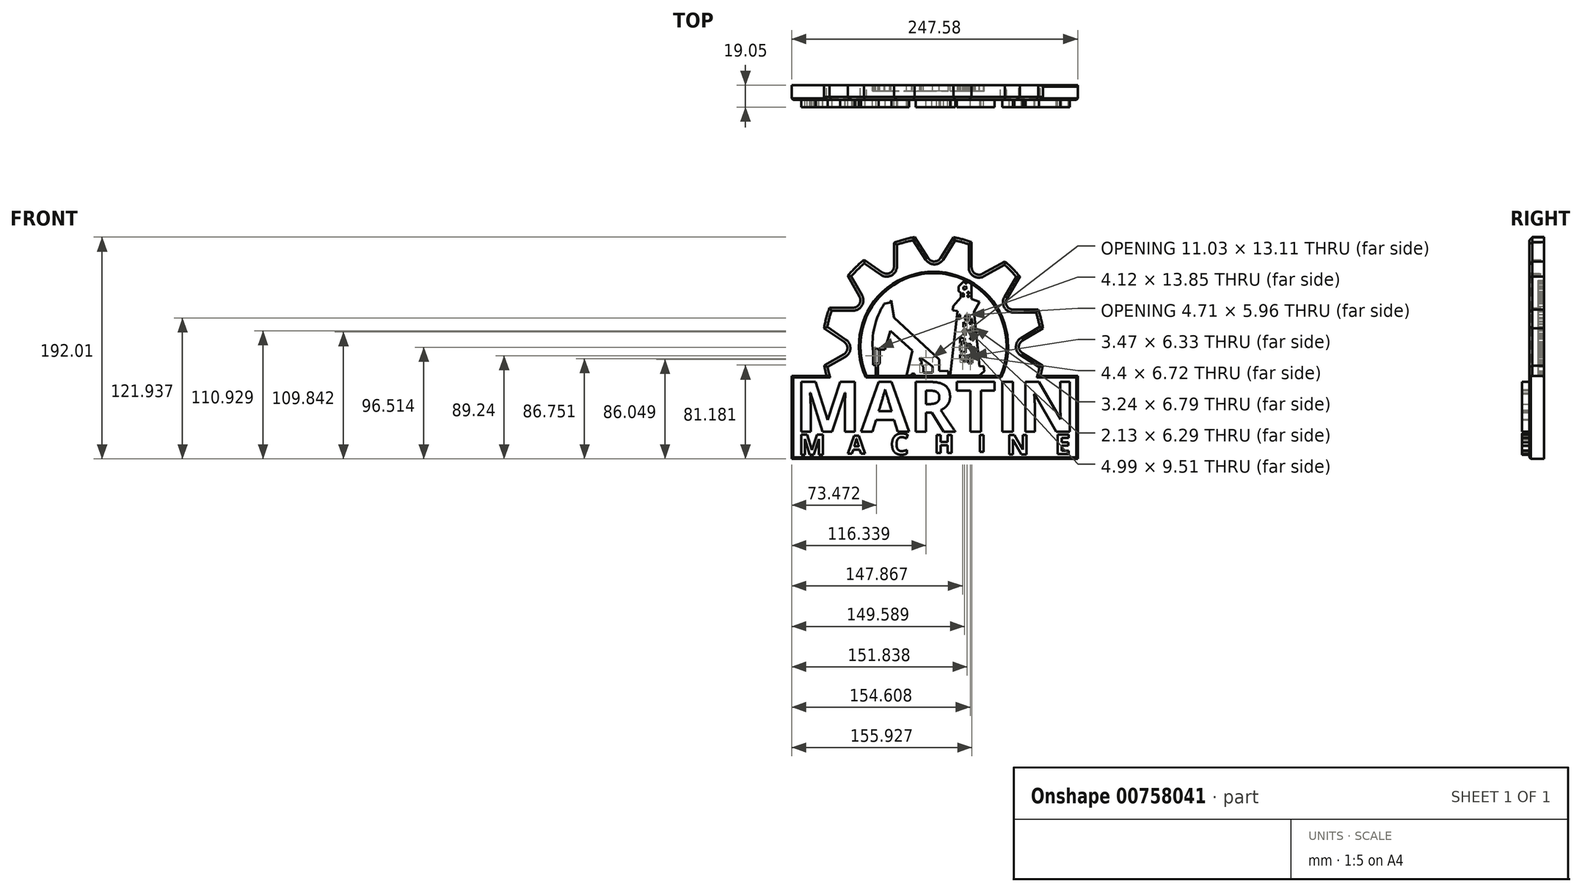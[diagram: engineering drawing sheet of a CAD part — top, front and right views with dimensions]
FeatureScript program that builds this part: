
annotation { "Feature Type Name" : "Feature", "Feature Type Description" : "" }
export const myFeature = defineFeature(function(context is Context, id is Id, definition is map)
    precondition{}
    {
        {
            var Q0;
            Q0=qCreatedBy(makeId("Front.planeOp"),FACE);
            var sketch = newSketch(context, id + "F0", { "sketchPlane" : qUnion([Q0])});
            skLineSegment(sketch, "E0.bottom", {"start": v(-69.87, -72.17) * mm, "end": v(-39.57, -72.17) * mm});
            skLineSegment(sketch, "E0.top", {"start": v(-69.87, -143.83) * mm, "end": v(177.7, -143.83) * mm});
            skLineSegment(sketch, "E0.left", {"start": v(-69.87, -72.17) * mm, "end": v(-69.87, -143.83) * mm});
            skLineSegment(sketch, "E0.right", {"start": v(177.7, -72.17) * mm, "end": v(177.7, -143.83) * mm});
            skArc(sketch, "E1", {"start": v(110.75, -72.17) * mm, "mid": v(52.91, 16.92) * mm, "end": v(-4.93, -72.17) * mm});
            skArc(sketch, "E2", {"start": v(145.39, -72.17) * mm, "mid": v(146.53, -67.65) * mm, "end": v(147.45, -63.07) * mm});
            skLineSegment(sketch, "E3.trimOffspring", {"start": v(-4.93, -72.17) * mm, "end": v(110.75, -72.17) * mm});
            skLineSegment(sketch, "E4.trimOffspring", {"start": v(145.39, -72.17) * mm, "end": v(177.7, -72.17) * mm});
            skLineSegment(sketch, "E5", {"start": v(-41.66, -62.9) * mm, "end": v(-24.87, -53.45) * mm});
            skLineSegment(sketch, "E6", {"start": v(-24.42, -42.66) * mm, "end": v(-41.82, -30.86) * mm});
            skLineSegment(sketch, "E7", {"start": v(-37.09, -13) * mm, "end": v(-16.73, -13) * mm});
            skLineSegment(sketch, "E8", {"start": v(-11.2, -3.53) * mm, "end": v(-21.33, 14.47) * mm});
            skLineSegment(sketch, "E9", {"start": v(-7.17, 28.47) * mm, "end": v(8.76, 17.56) * mm});
            skLineSegment(sketch, "E10", {"start": v(18.7, 22.8) * mm, "end": v(18.7, 43.3) * mm});
            skLineSegment(sketch, "E11", {"start": v(36.5, 48.18) * mm, "end": v(48.3, 29.98) * mm});
            skLineSegment(sketch, "E12", {"start": v(59.01, 30.05) * mm, "end": v(70.3, 48) * mm});
            skLineSegment(sketch, "E13", {"start": v(85.92, 43.74) * mm, "end": v(85.92, 21.91) * mm});
            skLineSegment(sketch, "E14", {"start": v(95.34, 16.35) * mm, "end": v(114.73, 27.04) * mm});
            skLineSegment(sketch, "E15", {"start": v(127.68, 13.8) * mm, "end": v(116.4, -4.98) * mm});
            skLineSegment(sketch, "E16", {"start": v(121.85, -14.6) * mm, "end": v(143.5, -14.6) * mm});
            skLineSegment(sketch, "E17", {"start": v(147.62, -30.7) * mm, "end": v(129.87, -41.41) * mm});
            skLineSegment(sketch, "E18", {"start": v(129.83, -52.26) * mm, "end": v(147.45, -63.07) * mm});
            skPoint(sketch, "E19.visualSharp", {"position": v(-15.93, -48.41) * mm});
            skArc(sketch, "E19.filletArc", {"start": v(-24.87, -53.45) * mm, "mid": v(-21.64, -48.18) * mm, "end": v(-24.42, -42.66) * mm});
            skPoint(sketch, "E20.visualSharp", {"position": v(-5.86, -13) * mm});
            skArc(sketch, "E20.filletArc", {"start": v(-16.73, -13) * mm, "mid": v(-11.25, -9.85) * mm, "end": v(-11.2, -3.53) * mm});
            skPoint(sketch, "E21.visualSharp", {"position": v(18.7, 10.76) * mm});
            skArc(sketch, "E21.filletArc", {"start": v(8.76, 17.56) * mm, "mid": v(15.3, 17.19) * mm, "end": v(18.7, 22.8) * mm});
            skPoint(sketch, "E22.visualSharp", {"position": v(53.72, 21.63) * mm});
            skArc(sketch, "E22.filletArc", {"start": v(48.3, 29.98) * mm, "mid": v(53.68, 27.08) * mm, "end": v(59.01, 30.05) * mm});
            skPoint(sketch, "E23.visualSharp", {"position": v(85.92, 11.16) * mm});
            skArc(sketch, "E23.filletArc", {"start": v(85.92, 21.91) * mm, "mid": v(89.04, 16.45) * mm, "end": v(95.34, 16.35) * mm});
            skPoint(sketch, "E24.visualSharp", {"position": v(110.64, -14.6) * mm});
            skArc(sketch, "E24.filletArc", {"start": v(116.4, -4.98) * mm, "mid": v(116.33, -11.38) * mm, "end": v(121.85, -14.6) * mm});
            skPoint(sketch, "E25.visualSharp", {"position": v(120.94, -46.8) * mm});
            skArc(sketch, "E25.filletArc", {"start": v(129.87, -41.41) * mm, "mid": v(126.8, -46.83) * mm, "end": v(129.83, -52.26) * mm});
            skArc(sketch, "E26.trimOffspring", {"start": v(-41.66, -62.9) * mm, "mid": v(-40.73, -67.56) * mm, "end": v(-39.57, -72.17) * mm});
            skArc(sketch, "E27.trimOffspring", {"start": v(-37.09, -13) * mm, "mid": v(-39.89, -21.81) * mm, "end": v(-41.82, -30.86) * mm});
            skArc(sketch, "E28.trimOffspring", {"start": v(-7.17, 28.47) * mm, "mid": v(-14.61, 21.84) * mm, "end": v(-21.33, 14.47) * mm});
            skArc(sketch, "E29.trimOffspring", {"start": v(36.5, 48.18) * mm, "mid": v(27.48, 46.17) * mm, "end": v(18.7, 43.3) * mm});
            skArc(sketch, "E30.trimOffspring", {"start": v(85.92, 43.74) * mm, "mid": v(78.2, 46.2) * mm, "end": v(70.3, 48) * mm});
            skArc(sketch, "E31.trimOffspring", {"start": v(127.68, 13.8) * mm, "mid": v(121.53, 20.74) * mm, "end": v(114.73, 27.04) * mm});
            skArc(sketch, "E32.trimOffspring", {"start": v(147.62, -30.7) * mm, "mid": v(145.9, -22.56) * mm, "end": v(143.5, -14.6) * mm});
            skSolve(sketch);
        }
        {
            var Q0;
            Q0=makeQuery(id+"F0.imprint","IMPRINT",FACE,{"disambiguationData":[TD([[makeQuery(id+"F0.imprint","IMPRINT",EDGE,{"derivedFrom":sQuery(id+"F0.wireOp",EDGE,"E0.bottom")}),-1.0]])]});
            extrude(context, id + "F1", {"entities" : qUnion([Q0]), "depth" : 12.7 * mm, "offsetDistance" : 25.4 * mm});
        }
        {
            var Q0;
            Q0=makeQuery(id+"F1.opExtrude","CAP_FACE",FACE,{"disambiguationData":[OSD([sQuery(id+"F0.wireOp",EDGE,"E0.bottom"),sQuery(id+"F0.wireOp",EDGE,"E0.top"),sQuery(id+"F0.wireOp",EDGE,"E0.left"),sQuery(id+"F0.wireOp",EDGE,"E0.right"),sQuery(id+"F0.wireOp",EDGE,"E1"),sQuery(id+"F0.wireOp",EDGE,"E2"),sQuery(id+"F0.wireOp",EDGE,"E3.trimOffspring"),sQuery(id+"F0.wireOp",EDGE,"E4.trimOffspring"),sQuery(id+"F0.wireOp",EDGE,"E5"),sQuery(id+"F0.wireOp",EDGE,"E6"),sQuery(id+"F0.wireOp",EDGE,"E7"),sQuery(id+"F0.wireOp",EDGE,"E8"),sQuery(id+"F0.wireOp",EDGE,"E9"),sQuery(id+"F0.wireOp",EDGE,"E10"),sQuery(id+"F0.wireOp",EDGE,"E11"),sQuery(id+"F0.wireOp",EDGE,"E12"),sQuery(id+"F0.wireOp",EDGE,"E13"),sQuery(id+"F0.wireOp",EDGE,"E14"),sQuery(id+"F0.wireOp",EDGE,"E15"),sQuery(id+"F0.wireOp",EDGE,"E16"),sQuery(id+"F0.wireOp",EDGE,"E17"),sQuery(id+"F0.wireOp",EDGE,"E18"),sQuery(id+"F0.wireOp",EDGE,"E19.filletArc"),sQuery(id+"F0.wireOp",EDGE,"E20.filletArc"),sQuery(id+"F0.wireOp",EDGE,"E21.filletArc"),sQuery(id+"F0.wireOp",EDGE,"E22.filletArc"),sQuery(id+"F0.wireOp",EDGE,"E23.filletArc"),sQuery(id+"F0.wireOp",EDGE,"E24.filletArc"),sQuery(id+"F0.wireOp",EDGE,"E25.filletArc"),sQuery(id+"F0.wireOp",EDGE,"E26.trimOffspring"),sQuery(id+"F0.wireOp",EDGE,"E27.trimOffspring"),sQuery(id+"F0.wireOp",EDGE,"E28.trimOffspring"),sQuery(id+"F0.wireOp",EDGE,"E29.trimOffspring"),sQuery(id+"F0.wireOp",EDGE,"E30.trimOffspring"),sQuery(id+"F0.wireOp",EDGE,"E31.trimOffspring"),sQuery(id+"F0.wireOp",EDGE,"E32.trimOffspring")])],"isStart":false});
            var sketch = newSketch(context, id + "F2", { "sketchPlane" : qUnion([Q0])});
            skText(sketch, "E33", { "text": "MARTIN", "fontName": "OpenSans-Bold.ttf"});
            const initialGuessF2  = {"E33": [-0.06698, -0.12048, 1, 0, 0.04361]};
            skSetInitialGuess(sketch, initialGuessF2);
            skSolve(sketch);
        }
        {
            var Q0;
            Q0=makeQuery(id+"F2.imprint","IMPRINT",FACE,{"disambiguationData":[TD([[makeQuery(id+"F2.imprint","IMPRINT",EDGE,{"derivedFrom":sQuery(id+"F2.wireOp",EDGE,"E33.sketch_text.stroke-0")}),-1.0]])]});
            var Q1;
            Q1=makeQuery(id+"F2.imprint","IMPRINT",FACE,{"disambiguationData":[TD([[makeQuery(id+"F2.imprint","IMPRINT",EDGE,{"derivedFrom":sQuery(id+"F2.wireOp",EDGE,"E33.sketch_text.stroke-19")}),-1.0]])]});
            var Q2;
            Q2=makeQuery(id+"F2.imprint","IMPRINT",FACE,{"disambiguationData":[TD([[makeQuery(id+"F2.imprint","IMPRINT",EDGE,{"derivedFrom":sQuery(id+"F2.wireOp",EDGE,"E33.sketch_text.stroke-31")}),-1.0]])]});
            var Q3;
            Q3=makeQuery(id+"F2.imprint","IMPRINT",FACE,{"disambiguationData":[TD([[makeQuery(id+"F2.imprint","IMPRINT",EDGE,{"derivedFrom":sQuery(id+"F2.wireOp",EDGE,"E33.sketch_text.stroke-50")}),-1.0]])]});
            var Q4;
            Q4=makeQuery(id+"F2.imprint","IMPRINT",FACE,{"disambiguationData":[TD([[makeQuery(id+"F2.imprint","IMPRINT",EDGE,{"derivedFrom":sQuery(id+"F2.wireOp",EDGE,"E33.sketch_text.stroke-58")}),-1.0]])]});
            var Q5;
            Q5=makeQuery(id+"F2.imprint","IMPRINT",FACE,{"disambiguationData":[TD([[makeQuery(id+"F2.imprint","IMPRINT",EDGE,{"derivedFrom":sQuery(id+"F2.wireOp",EDGE,"E33.sketch_text.stroke-62")}),-1.0]])]});
            extrude(context, id + "F3", {"entities" : qUnion([Q0, Q1, Q2, Q3, Q4, Q5]), "operationType" : NewBodyOperationType.ADD, "depth" : 6.35 * mm, "offsetDistance" : 25.4 * mm});
        }
        {
            var Q0;
            {var subQ0=sQuery(id+"F0.wireOp",EDGE,"E15");var subQ1=sQuery(id+"F0.wireOp",EDGE,"E14");var subQ2=sQuery(id+"F0.wireOp",EDGE,"E12");var subQ3=sQuery(id+"F0.wireOp",EDGE,"E11");var subQ4=sQuery(id+"F0.wireOp",EDGE,"E10");var subQ5=sQuery(id+"F0.wireOp",EDGE,"E9");var subQ6=sQuery(id+"F0.wireOp",EDGE,"E8");var subQ7=sQuery(id+"F0.wireOp",EDGE,"E7");var subQ8=sQuery(id+"F0.wireOp",EDGE,"E0.left");var subQ9=sQuery(id+"F0.wireOp",EDGE,"E0.top");var subQ10=sQuery(id+"F0.wireOp",EDGE,"E0.right");var subQ11=sQuery(id+"F0.wireOp",EDGE,"E0.bottom");var subQ12=sQuery(id+"F0.wireOp",EDGE,"E6");var subQ13=sQuery(id+"F0.wireOp",EDGE,"E1");var subQ14=sQuery(id+"F0.wireOp",EDGE,"E2");var subQ15=sQuery(id+"F0.wireOp",EDGE,"E3.trimOffspring");var subQ16=sQuery(id+"F0.wireOp",EDGE,"E4.trimOffspring");var subQ17=sQuery(id+"F0.wireOp",EDGE,"E5");var subQ18=sQuery(id+"F0.wireOp",EDGE,"E13");var subQ19=sQuery(id+"F0.wireOp",EDGE,"E22.filletArc");var subQ20=sQuery(id+"F0.wireOp",EDGE,"E25.filletArc");var subQ21=sQuery(id+"F0.wireOp",EDGE,"E26.trimOffspring");var subQ22=sQuery(id+"F0.wireOp",EDGE,"E16");var subQ23=sQuery(id+"F0.wireOp",EDGE,"E27.trimOffspring");var subQ24=sQuery(id+"F0.wireOp",EDGE,"E17");var subQ25=sQuery(id+"F0.wireOp",EDGE,"E28.trimOffspring");var subQ26=sQuery(id+"F0.wireOp",EDGE,"E18");var subQ27=sQuery(id+"F0.wireOp",EDGE,"E29.trimOffspring");var subQ28=sQuery(id+"F0.wireOp",EDGE,"E19.filletArc");var subQ29=sQuery(id+"F0.wireOp",EDGE,"E30.trimOffspring");var subQ30=sQuery(id+"F0.wireOp",EDGE,"E20.filletArc");var subQ31=sQuery(id+"F0.wireOp",EDGE,"E31.trimOffspring");var subQ32=sQuery(id+"F0.wireOp",EDGE,"E21.filletArc");var subQ33=sQuery(id+"F0.wireOp",EDGE,"E32.trimOffspring");var subQ34=sQuery(id+"F0.wireOp",EDGE,"E23.filletArc");var subQ35=sQuery(id+"F0.wireOp",EDGE,"E24.filletArc");Q0=makeQuery(id+"F3.boolean.opBoolean","SPLIT",FACE,{"disambiguationData":[TD([makeQuery(id+"F1.opExtrude","SWEPT_FACE",FACE,{"disambiguationData":[OSD([subQ11])]})])],"derivedFrom":makeQuery(id+"F1.opExtrude","CAP_FACE",FACE,{"disambiguationData":[OSD([subQ11,subQ9,subQ8,subQ10,subQ13,subQ14,subQ15,subQ16,subQ17,subQ12,subQ7,subQ6,subQ5,subQ4,subQ3,subQ2,subQ18,subQ1,subQ0,subQ22,subQ24,subQ26,subQ28,subQ30,subQ32,subQ19,subQ34,subQ35,subQ20,subQ21,subQ23,subQ25,subQ27,subQ29,subQ31,subQ33])],"isStart":false})});}
            var sketch = newSketch(context, id + "F4", { "sketchPlane" : qUnion([Q0])});
            skText(sketch, "E34", { "text": "M", "fontName": "OpenSans-Bold.ttf"});
            const initialGuessF4  = {"E34": [-0.06372, -0.14035, 1, 0, 0.0175]};
            skSetInitialGuess(sketch, initialGuessF4);
            skSolve(sketch);
        }
        {
            var Q0;
            Q0 = qSketchRegion(id + "F4", true);
            extrude(context, id + "F5", {"entities" : qUnion([Q0]), "operationType" : NewBodyOperationType.ADD, "depth" : 6.35 * mm, "offsetDistance" : 25.4 * mm});
        }
        {
            var Q0;
            {var subQ0=sQuery(id+"F0.wireOp",EDGE,"E15");var subQ1=sQuery(id+"F0.wireOp",EDGE,"E14");var subQ2=sQuery(id+"F0.wireOp",EDGE,"E12");var subQ3=sQuery(id+"F0.wireOp",EDGE,"E11");var subQ4=sQuery(id+"F0.wireOp",EDGE,"E10");var subQ5=sQuery(id+"F0.wireOp",EDGE,"E9");var subQ6=sQuery(id+"F0.wireOp",EDGE,"E8");var subQ7=sQuery(id+"F0.wireOp",EDGE,"E7");var subQ8=sQuery(id+"F0.wireOp",EDGE,"E0.left");var subQ9=sQuery(id+"F0.wireOp",EDGE,"E0.top");var subQ10=sQuery(id+"F0.wireOp",EDGE,"E0.right");var subQ11=sQuery(id+"F0.wireOp",EDGE,"E0.bottom");var subQ12=sQuery(id+"F0.wireOp",EDGE,"E6");var subQ13=sQuery(id+"F0.wireOp",EDGE,"E1");var subQ14=sQuery(id+"F0.wireOp",EDGE,"E2");var subQ15=sQuery(id+"F0.wireOp",EDGE,"E3.trimOffspring");var subQ16=sQuery(id+"F0.wireOp",EDGE,"E4.trimOffspring");var subQ17=sQuery(id+"F0.wireOp",EDGE,"E5");var subQ18=sQuery(id+"F0.wireOp",EDGE,"E13");var subQ19=sQuery(id+"F0.wireOp",EDGE,"E22.filletArc");var subQ20=sQuery(id+"F0.wireOp",EDGE,"E25.filletArc");var subQ21=sQuery(id+"F0.wireOp",EDGE,"E26.trimOffspring");var subQ22=sQuery(id+"F0.wireOp",EDGE,"E16");var subQ23=sQuery(id+"F0.wireOp",EDGE,"E27.trimOffspring");var subQ24=sQuery(id+"F0.wireOp",EDGE,"E17");var subQ25=sQuery(id+"F0.wireOp",EDGE,"E28.trimOffspring");var subQ26=sQuery(id+"F0.wireOp",EDGE,"E18");var subQ27=sQuery(id+"F0.wireOp",EDGE,"E29.trimOffspring");var subQ28=sQuery(id+"F0.wireOp",EDGE,"E19.filletArc");var subQ29=sQuery(id+"F0.wireOp",EDGE,"E30.trimOffspring");var subQ30=sQuery(id+"F0.wireOp",EDGE,"E20.filletArc");var subQ31=sQuery(id+"F0.wireOp",EDGE,"E31.trimOffspring");var subQ32=sQuery(id+"F0.wireOp",EDGE,"E21.filletArc");var subQ33=sQuery(id+"F0.wireOp",EDGE,"E32.trimOffspring");var subQ34=sQuery(id+"F0.wireOp",EDGE,"E23.filletArc");var subQ35=sQuery(id+"F0.wireOp",EDGE,"E24.filletArc");Q0=makeQuery(id+"F3.boolean.opBoolean","SPLIT",FACE,{"disambiguationData":[TD([makeQuery(id+"F1.opExtrude","SWEPT_FACE",FACE,{"disambiguationData":[OSD([subQ11])]})])],"derivedFrom":makeQuery(id+"F1.opExtrude","CAP_FACE",FACE,{"disambiguationData":[OSD([subQ11,subQ9,subQ8,subQ10,subQ13,subQ14,subQ15,subQ16,subQ17,subQ12,subQ7,subQ6,subQ5,subQ4,subQ3,subQ2,subQ18,subQ1,subQ0,subQ22,subQ24,subQ26,subQ28,subQ30,subQ32,subQ19,subQ34,subQ35,subQ20,subQ21,subQ23,subQ25,subQ27,subQ29,subQ31,subQ33])],"isStart":false})});}
            var sketch = newSketch(context, id + "F6", { "sketchPlane" : qUnion([Q0])});
            skText(sketch, "E35", { "text": "A", "fontName": "OpenSans-Bold.ttf"});
            const initialGuessF6  = {"E35": [-0.0213, -0.13946, 1, 0, 0.01572]};
            skSetInitialGuess(sketch, initialGuessF6);
            skSolve(sketch);
        }
        {
            var Q0;
            Q0 = qSketchRegion(id + "F6", true);
            extrude(context, id + "F7", {"entities" : qUnion([Q0]), "operationType" : NewBodyOperationType.ADD, "depth" : 6.35 * mm, "offsetDistance" : 25.4 * mm});
        }
        {
            var Q0;
            {var subQ40=sQuery(id+"F0.wireOp",EDGE,"E15");var subQ42=sQuery(id+"F0.wireOp",EDGE,"E14");var subQ44=sQuery(id+"F0.wireOp",EDGE,"E12");var subQ46=sQuery(id+"F0.wireOp",EDGE,"E11");var subQ48=sQuery(id+"F0.wireOp",EDGE,"E10");var subQ50=sQuery(id+"F0.wireOp",EDGE,"E9");var subQ52=sQuery(id+"F0.wireOp",EDGE,"E8");var subQ54=sQuery(id+"F0.wireOp",EDGE,"E7");var subQ56=sQuery(id+"F0.wireOp",EDGE,"E0.left");var subQ59=sQuery(id+"F0.wireOp",EDGE,"E0.top");var subQ61=sQuery(id+"F0.wireOp",EDGE,"E0.right");var subQ64=sQuery(id+"F0.wireOp",EDGE,"E0.bottom");var subQ65=makeQuery(id+"F1.opExtrude","SWEPT_FACE",FACE,{"disambiguationData":[OSD([subQ64])]});var subQ66=sQuery(id+"F0.wireOp",EDGE,"E6");var subQ68=sQuery(id+"F0.wireOp",EDGE,"E1");var subQ70=sQuery(id+"F0.wireOp",EDGE,"E2");var subQ72=sQuery(id+"F0.wireOp",EDGE,"E3.trimOffspring");var subQ74=sQuery(id+"F0.wireOp",EDGE,"E4.trimOffspring");var subQ76=sQuery(id+"F0.wireOp",EDGE,"E5");var subQ78=sQuery(id+"F0.wireOp",EDGE,"E13");var subQ81=sQuery(id+"F0.wireOp",EDGE,"E22.filletArc");var subQ84=sQuery(id+"F0.wireOp",EDGE,"E25.filletArc");var subQ88=sQuery(id+"F0.wireOp",EDGE,"E26.trimOffspring");var subQ91=sQuery(id+"F0.wireOp",EDGE,"E16");var subQ94=sQuery(id+"F0.wireOp",EDGE,"E27.trimOffspring");var subQ97=sQuery(id+"F0.wireOp",EDGE,"E17");var subQ100=sQuery(id+"F0.wireOp",EDGE,"E28.trimOffspring");var subQ103=sQuery(id+"F0.wireOp",EDGE,"E18");var subQ106=sQuery(id+"F0.wireOp",EDGE,"E29.trimOffspring");var subQ109=sQuery(id+"F0.wireOp",EDGE,"E19.filletArc");var subQ112=sQuery(id+"F0.wireOp",EDGE,"E30.trimOffspring");var subQ115=sQuery(id+"F0.wireOp",EDGE,"E20.filletArc");var subQ118=sQuery(id+"F0.wireOp",EDGE,"E31.trimOffspring");var subQ121=sQuery(id+"F0.wireOp",EDGE,"E21.filletArc");var subQ124=sQuery(id+"F0.wireOp",EDGE,"E32.trimOffspring");var subQ127=sQuery(id+"F0.wireOp",EDGE,"E23.filletArc");var subQ129=sQuery(id+"F0.wireOp",EDGE,"E24.filletArc");Q0=makeQuery(id+"F7.boolean.opBoolean","SPLIT",FACE,{"disambiguationData":[TD([subQ65])],"derivedFrom":makeQuery(id+"F3.boolean.opBoolean","SPLIT",FACE,{"disambiguationData":[TD([subQ65])],"derivedFrom":makeQuery(id+"F1.opExtrude","CAP_FACE",FACE,{"disambiguationData":[OSD([subQ64,subQ59,subQ56,subQ61,subQ68,subQ70,subQ72,subQ74,subQ76,subQ66,subQ54,subQ52,subQ50,subQ48,subQ46,subQ44,subQ78,subQ42,subQ40,subQ91,subQ97,subQ103,subQ109,subQ115,subQ121,subQ81,subQ127,subQ129,subQ84,subQ88,subQ94,subQ100,subQ106,subQ112,subQ118,subQ124])],"isStart":false})})});}
            var sketch = newSketch(context, id + "F8", { "sketchPlane" : qUnion([Q0])});
            skText(sketch, "E36", { "text": "C", "fontName": "OpenSans-Bold.ttf"});
            const initialGuessF8  = {"E36": [0.0155, -0.14006, 1, 0, 0.0181]};
            skSetInitialGuess(sketch, initialGuessF8);
            skSolve(sketch);
        }
        {
            var Q0;
            Q0 = qSketchRegion(id + "F8", true);
            extrude(context, id + "F9", {"entities" : qUnion([Q0]), "operationType" : NewBodyOperationType.ADD, "depth" : 6.35 * mm, "offsetDistance" : 25.4 * mm});
        }
        {
            var Q0;
            {var subQ40=sQuery(id+"F0.wireOp",EDGE,"E15");var subQ42=sQuery(id+"F0.wireOp",EDGE,"E14");var subQ44=sQuery(id+"F0.wireOp",EDGE,"E12");var subQ46=sQuery(id+"F0.wireOp",EDGE,"E11");var subQ48=sQuery(id+"F0.wireOp",EDGE,"E10");var subQ50=sQuery(id+"F0.wireOp",EDGE,"E9");var subQ52=sQuery(id+"F0.wireOp",EDGE,"E8");var subQ54=sQuery(id+"F0.wireOp",EDGE,"E7");var subQ56=sQuery(id+"F0.wireOp",EDGE,"E0.left");var subQ59=sQuery(id+"F0.wireOp",EDGE,"E0.top");var subQ61=sQuery(id+"F0.wireOp",EDGE,"E0.right");var subQ64=sQuery(id+"F0.wireOp",EDGE,"E0.bottom");var subQ65=makeQuery(id+"F1.opExtrude","SWEPT_FACE",FACE,{"disambiguationData":[OSD([subQ64])]});var subQ66=sQuery(id+"F0.wireOp",EDGE,"E6");var subQ68=sQuery(id+"F0.wireOp",EDGE,"E1");var subQ70=sQuery(id+"F0.wireOp",EDGE,"E2");var subQ72=sQuery(id+"F0.wireOp",EDGE,"E3.trimOffspring");var subQ74=sQuery(id+"F0.wireOp",EDGE,"E4.trimOffspring");var subQ76=sQuery(id+"F0.wireOp",EDGE,"E5");var subQ78=sQuery(id+"F0.wireOp",EDGE,"E13");var subQ81=sQuery(id+"F0.wireOp",EDGE,"E22.filletArc");var subQ84=sQuery(id+"F0.wireOp",EDGE,"E25.filletArc");var subQ88=sQuery(id+"F0.wireOp",EDGE,"E26.trimOffspring");var subQ91=sQuery(id+"F0.wireOp",EDGE,"E16");var subQ94=sQuery(id+"F0.wireOp",EDGE,"E27.trimOffspring");var subQ97=sQuery(id+"F0.wireOp",EDGE,"E17");var subQ100=sQuery(id+"F0.wireOp",EDGE,"E28.trimOffspring");var subQ103=sQuery(id+"F0.wireOp",EDGE,"E18");var subQ106=sQuery(id+"F0.wireOp",EDGE,"E29.trimOffspring");var subQ109=sQuery(id+"F0.wireOp",EDGE,"E19.filletArc");var subQ112=sQuery(id+"F0.wireOp",EDGE,"E30.trimOffspring");var subQ115=sQuery(id+"F0.wireOp",EDGE,"E20.filletArc");var subQ118=sQuery(id+"F0.wireOp",EDGE,"E31.trimOffspring");var subQ121=sQuery(id+"F0.wireOp",EDGE,"E21.filletArc");var subQ124=sQuery(id+"F0.wireOp",EDGE,"E32.trimOffspring");var subQ127=sQuery(id+"F0.wireOp",EDGE,"E23.filletArc");var subQ129=sQuery(id+"F0.wireOp",EDGE,"E24.filletArc");Q0=makeQuery(id+"F7.boolean.opBoolean","SPLIT",FACE,{"disambiguationData":[TD([subQ65])],"derivedFrom":makeQuery(id+"F3.boolean.opBoolean","SPLIT",FACE,{"disambiguationData":[TD([subQ65])],"derivedFrom":makeQuery(id+"F1.opExtrude","CAP_FACE",FACE,{"disambiguationData":[OSD([subQ64,subQ59,subQ56,subQ61,subQ68,subQ70,subQ72,subQ74,subQ76,subQ66,subQ54,subQ52,subQ50,subQ48,subQ46,subQ44,subQ78,subQ42,subQ40,subQ91,subQ97,subQ103,subQ109,subQ115,subQ121,subQ81,subQ127,subQ129,subQ84,subQ88,subQ94,subQ100,subQ106,subQ112,subQ118,subQ124])],"isStart":false})})});}
            var sketch = newSketch(context, id + "F10", { "sketchPlane" : qUnion([Q0])});
            skText(sketch, "E37", { "text": "H", "fontName": "OpenSans-Bold.ttf"});
            const initialGuessF10  = {"E37": [0.05377, -0.13887, 1, 0, 0.01572]};
            skSetInitialGuess(sketch, initialGuessF10);
            skSolve(sketch);
        }
        {
            var Q0;
            Q0 = qSketchRegion(id + "F10", true);
            extrude(context, id + "F11", {"entities" : qUnion([Q0]), "operationType" : NewBodyOperationType.ADD, "depth" : 6.35 * mm, "offsetDistance" : 25.4 * mm});
        }
        {
            var Q0;
            {var subQ40=sQuery(id+"F0.wireOp",EDGE,"E15");var subQ42=sQuery(id+"F0.wireOp",EDGE,"E14");var subQ44=sQuery(id+"F0.wireOp",EDGE,"E12");var subQ46=sQuery(id+"F0.wireOp",EDGE,"E11");var subQ48=sQuery(id+"F0.wireOp",EDGE,"E10");var subQ50=sQuery(id+"F0.wireOp",EDGE,"E9");var subQ52=sQuery(id+"F0.wireOp",EDGE,"E8");var subQ54=sQuery(id+"F0.wireOp",EDGE,"E7");var subQ56=sQuery(id+"F0.wireOp",EDGE,"E0.left");var subQ59=sQuery(id+"F0.wireOp",EDGE,"E0.top");var subQ61=sQuery(id+"F0.wireOp",EDGE,"E0.right");var subQ64=sQuery(id+"F0.wireOp",EDGE,"E0.bottom");var subQ65=makeQuery(id+"F1.opExtrude","SWEPT_FACE",FACE,{"disambiguationData":[OSD([subQ64])]});var subQ66=sQuery(id+"F0.wireOp",EDGE,"E6");var subQ68=sQuery(id+"F0.wireOp",EDGE,"E1");var subQ70=sQuery(id+"F0.wireOp",EDGE,"E2");var subQ72=sQuery(id+"F0.wireOp",EDGE,"E3.trimOffspring");var subQ74=sQuery(id+"F0.wireOp",EDGE,"E4.trimOffspring");var subQ76=sQuery(id+"F0.wireOp",EDGE,"E5");var subQ78=sQuery(id+"F0.wireOp",EDGE,"E13");var subQ81=sQuery(id+"F0.wireOp",EDGE,"E22.filletArc");var subQ84=sQuery(id+"F0.wireOp",EDGE,"E25.filletArc");var subQ88=sQuery(id+"F0.wireOp",EDGE,"E26.trimOffspring");var subQ91=sQuery(id+"F0.wireOp",EDGE,"E16");var subQ94=sQuery(id+"F0.wireOp",EDGE,"E27.trimOffspring");var subQ97=sQuery(id+"F0.wireOp",EDGE,"E17");var subQ100=sQuery(id+"F0.wireOp",EDGE,"E28.trimOffspring");var subQ103=sQuery(id+"F0.wireOp",EDGE,"E18");var subQ106=sQuery(id+"F0.wireOp",EDGE,"E29.trimOffspring");var subQ109=sQuery(id+"F0.wireOp",EDGE,"E19.filletArc");var subQ112=sQuery(id+"F0.wireOp",EDGE,"E30.trimOffspring");var subQ115=sQuery(id+"F0.wireOp",EDGE,"E20.filletArc");var subQ118=sQuery(id+"F0.wireOp",EDGE,"E31.trimOffspring");var subQ121=sQuery(id+"F0.wireOp",EDGE,"E21.filletArc");var subQ124=sQuery(id+"F0.wireOp",EDGE,"E32.trimOffspring");var subQ127=sQuery(id+"F0.wireOp",EDGE,"E23.filletArc");var subQ129=sQuery(id+"F0.wireOp",EDGE,"E24.filletArc");Q0=makeQuery(id+"F7.boolean.opBoolean","SPLIT",FACE,{"disambiguationData":[TD([subQ65])],"derivedFrom":makeQuery(id+"F3.boolean.opBoolean","SPLIT",FACE,{"disambiguationData":[TD([subQ65])],"derivedFrom":makeQuery(id+"F1.opExtrude","CAP_FACE",FACE,{"disambiguationData":[OSD([subQ64,subQ59,subQ56,subQ61,subQ68,subQ70,subQ72,subQ74,subQ76,subQ66,subQ54,subQ52,subQ50,subQ48,subQ46,subQ44,subQ78,subQ42,subQ40,subQ91,subQ97,subQ103,subQ109,subQ115,subQ121,subQ81,subQ127,subQ129,subQ84,subQ88,subQ94,subQ100,subQ106,subQ112,subQ118,subQ124])],"isStart":false})})});}
            var sketch = newSketch(context, id + "F12", { "sketchPlane" : qUnion([Q0])});
            skText(sketch, "E38", { "text": "I", "fontName": "OpenSans-Bold.ttf"});
            const initialGuessF12  = {"E38": [0.09122, -0.13776, 1, 0, 0.01454]};
            skSetInitialGuess(sketch, initialGuessF12);
            skSolve(sketch);
        }
        {
            var Q0;
            Q0=makeQuery(id+"F12.imprint","IMPRINT",FACE,{"disambiguationData":[TD([[makeQuery(id+"F12.imprint","IMPRINT",EDGE,{"derivedFrom":sQuery(id+"F12.wireOp",EDGE,"E38.sketch_text.stroke-0")}),-1.0]])]});
            extrude(context, id + "F13", {"entities" : qUnion([Q0]), "operationType" : NewBodyOperationType.ADD, "depth" : 6.35 * mm, "offsetDistance" : 25.4 * mm});
        }
        {
            var Q0;
            {var subQ40=sQuery(id+"F0.wireOp",EDGE,"E15");var subQ42=sQuery(id+"F0.wireOp",EDGE,"E14");var subQ44=sQuery(id+"F0.wireOp",EDGE,"E12");var subQ46=sQuery(id+"F0.wireOp",EDGE,"E11");var subQ48=sQuery(id+"F0.wireOp",EDGE,"E10");var subQ50=sQuery(id+"F0.wireOp",EDGE,"E9");var subQ52=sQuery(id+"F0.wireOp",EDGE,"E8");var subQ54=sQuery(id+"F0.wireOp",EDGE,"E7");var subQ56=sQuery(id+"F0.wireOp",EDGE,"E0.left");var subQ59=sQuery(id+"F0.wireOp",EDGE,"E0.top");var subQ61=sQuery(id+"F0.wireOp",EDGE,"E0.right");var subQ64=sQuery(id+"F0.wireOp",EDGE,"E0.bottom");var subQ65=makeQuery(id+"F1.opExtrude","SWEPT_FACE",FACE,{"disambiguationData":[OSD([subQ64])]});var subQ66=sQuery(id+"F0.wireOp",EDGE,"E6");var subQ68=sQuery(id+"F0.wireOp",EDGE,"E1");var subQ70=sQuery(id+"F0.wireOp",EDGE,"E2");var subQ72=sQuery(id+"F0.wireOp",EDGE,"E3.trimOffspring");var subQ74=sQuery(id+"F0.wireOp",EDGE,"E4.trimOffspring");var subQ76=sQuery(id+"F0.wireOp",EDGE,"E5");var subQ78=sQuery(id+"F0.wireOp",EDGE,"E13");var subQ81=sQuery(id+"F0.wireOp",EDGE,"E22.filletArc");var subQ84=sQuery(id+"F0.wireOp",EDGE,"E25.filletArc");var subQ88=sQuery(id+"F0.wireOp",EDGE,"E26.trimOffspring");var subQ91=sQuery(id+"F0.wireOp",EDGE,"E16");var subQ94=sQuery(id+"F0.wireOp",EDGE,"E27.trimOffspring");var subQ97=sQuery(id+"F0.wireOp",EDGE,"E17");var subQ100=sQuery(id+"F0.wireOp",EDGE,"E28.trimOffspring");var subQ103=sQuery(id+"F0.wireOp",EDGE,"E18");var subQ106=sQuery(id+"F0.wireOp",EDGE,"E29.trimOffspring");var subQ109=sQuery(id+"F0.wireOp",EDGE,"E19.filletArc");var subQ112=sQuery(id+"F0.wireOp",EDGE,"E30.trimOffspring");var subQ115=sQuery(id+"F0.wireOp",EDGE,"E20.filletArc");var subQ118=sQuery(id+"F0.wireOp",EDGE,"E31.trimOffspring");var subQ121=sQuery(id+"F0.wireOp",EDGE,"E21.filletArc");var subQ124=sQuery(id+"F0.wireOp",EDGE,"E32.trimOffspring");var subQ127=sQuery(id+"F0.wireOp",EDGE,"E23.filletArc");var subQ129=sQuery(id+"F0.wireOp",EDGE,"E24.filletArc");Q0=makeQuery(id+"F7.boolean.opBoolean","SPLIT",FACE,{"disambiguationData":[TD([subQ65])],"derivedFrom":makeQuery(id+"F3.boolean.opBoolean","SPLIT",FACE,{"disambiguationData":[TD([subQ65])],"derivedFrom":makeQuery(id+"F1.opExtrude","CAP_FACE",FACE,{"disambiguationData":[OSD([subQ64,subQ59,subQ56,subQ61,subQ68,subQ70,subQ72,subQ74,subQ76,subQ66,subQ54,subQ52,subQ50,subQ48,subQ46,subQ44,subQ78,subQ42,subQ40,subQ91,subQ97,subQ103,subQ109,subQ115,subQ121,subQ81,subQ127,subQ129,subQ84,subQ88,subQ94,subQ100,subQ106,subQ112,subQ118,subQ124])],"isStart":false})})});}
            var sketch = newSketch(context, id + "F14", { "sketchPlane" : qUnion([Q0])});
            skText(sketch, "E39", { "text": "N", "fontName": "OpenSans-Bold.ttf"});
            const initialGuessF14  = {"E39": [0.11641, -0.13995, 1, 0, 0.01678]};
            skSetInitialGuess(sketch, initialGuessF14);
            skSolve(sketch);
        }
        {
            var Q0;
            Q0=makeQuery(id+"F14.imprint","IMPRINT",FACE,{"disambiguationData":[TD([[makeQuery(id+"F14.imprint","IMPRINT",EDGE,{"derivedFrom":sQuery(id+"F14.wireOp",EDGE,"E39.sketch_text.stroke-0")}),-1.0]])]});
            extrude(context, id + "F15", {"entities" : qUnion([Q0]), "operationType" : NewBodyOperationType.ADD, "depth" : 6.35 * mm, "offsetDistance" : 25.4 * mm});
        }
        {
            var Q0;
            {var subQ40=sQuery(id+"F0.wireOp",EDGE,"E15");var subQ42=sQuery(id+"F0.wireOp",EDGE,"E14");var subQ44=sQuery(id+"F0.wireOp",EDGE,"E12");var subQ46=sQuery(id+"F0.wireOp",EDGE,"E11");var subQ48=sQuery(id+"F0.wireOp",EDGE,"E10");var subQ50=sQuery(id+"F0.wireOp",EDGE,"E9");var subQ52=sQuery(id+"F0.wireOp",EDGE,"E8");var subQ54=sQuery(id+"F0.wireOp",EDGE,"E7");var subQ56=sQuery(id+"F0.wireOp",EDGE,"E0.left");var subQ59=sQuery(id+"F0.wireOp",EDGE,"E0.top");var subQ61=sQuery(id+"F0.wireOp",EDGE,"E0.right");var subQ64=sQuery(id+"F0.wireOp",EDGE,"E0.bottom");var subQ65=makeQuery(id+"F1.opExtrude","SWEPT_FACE",FACE,{"disambiguationData":[OSD([subQ64])]});var subQ66=sQuery(id+"F0.wireOp",EDGE,"E6");var subQ68=sQuery(id+"F0.wireOp",EDGE,"E1");var subQ70=sQuery(id+"F0.wireOp",EDGE,"E2");var subQ72=sQuery(id+"F0.wireOp",EDGE,"E3.trimOffspring");var subQ74=sQuery(id+"F0.wireOp",EDGE,"E4.trimOffspring");var subQ76=sQuery(id+"F0.wireOp",EDGE,"E5");var subQ78=sQuery(id+"F0.wireOp",EDGE,"E13");var subQ81=sQuery(id+"F0.wireOp",EDGE,"E22.filletArc");var subQ84=sQuery(id+"F0.wireOp",EDGE,"E25.filletArc");var subQ88=sQuery(id+"F0.wireOp",EDGE,"E26.trimOffspring");var subQ91=sQuery(id+"F0.wireOp",EDGE,"E16");var subQ94=sQuery(id+"F0.wireOp",EDGE,"E27.trimOffspring");var subQ97=sQuery(id+"F0.wireOp",EDGE,"E17");var subQ100=sQuery(id+"F0.wireOp",EDGE,"E28.trimOffspring");var subQ103=sQuery(id+"F0.wireOp",EDGE,"E18");var subQ106=sQuery(id+"F0.wireOp",EDGE,"E29.trimOffspring");var subQ109=sQuery(id+"F0.wireOp",EDGE,"E19.filletArc");var subQ112=sQuery(id+"F0.wireOp",EDGE,"E30.trimOffspring");var subQ115=sQuery(id+"F0.wireOp",EDGE,"E20.filletArc");var subQ118=sQuery(id+"F0.wireOp",EDGE,"E31.trimOffspring");var subQ121=sQuery(id+"F0.wireOp",EDGE,"E21.filletArc");var subQ124=sQuery(id+"F0.wireOp",EDGE,"E32.trimOffspring");var subQ127=sQuery(id+"F0.wireOp",EDGE,"E23.filletArc");var subQ129=sQuery(id+"F0.wireOp",EDGE,"E24.filletArc");Q0=makeQuery(id+"F7.boolean.opBoolean","SPLIT",FACE,{"disambiguationData":[TD([subQ65])],"derivedFrom":makeQuery(id+"F3.boolean.opBoolean","SPLIT",FACE,{"disambiguationData":[TD([subQ65])],"derivedFrom":makeQuery(id+"F1.opExtrude","CAP_FACE",FACE,{"disambiguationData":[OSD([subQ64,subQ59,subQ56,subQ61,subQ68,subQ70,subQ72,subQ74,subQ76,subQ66,subQ54,subQ52,subQ50,subQ48,subQ46,subQ44,subQ78,subQ42,subQ40,subQ91,subQ97,subQ103,subQ109,subQ115,subQ121,subQ81,subQ127,subQ129,subQ84,subQ88,subQ94,subQ100,subQ106,subQ112,subQ118,subQ124])],"isStart":false})})});}
            var sketch = newSketch(context, id + "F16", { "sketchPlane" : qUnion([Q0])});
            skText(sketch, "E40", { "text": "E", "fontName": "OpenSans-Bold.ttf"});
            const initialGuessF16  = {"E40": [0.15816, -0.13974, 1, 0, 0.017]};
            skSetInitialGuess(sketch, initialGuessF16);
            skSolve(sketch);
        }
        {
            var Q0;
            Q0 = qSketchRegion(id + "F16", true);
            extrude(context, id + "F17", {"entities" : qUnion([Q0]), "operationType" : NewBodyOperationType.ADD, "depth" : 6.35 * mm, "offsetDistance" : 25.4 * mm});
        }
        {
            var Q0;
            Q0=makeQuery(id+"F1.opExtrude","CAP_EDGE",EDGE,{"disambiguationData":[OSD([sQuery(id+"F0.wireOp",EDGE,"E27.trimOffspring")])],"isStart":false});
            var Q1;
            Q1=makeQuery(id+"F1.opExtrude","CAP_EDGE",EDGE,{"disambiguationData":[OSD([sQuery(id+"F0.wireOp",EDGE,"E26.trimOffspring")])],"isStart":false});
            var Q2;
            Q2=makeQuery(id+"F1.opExtrude","CAP_EDGE",EDGE,{"disambiguationData":[OSD([sQuery(id+"F0.wireOp",EDGE,"E28.trimOffspring")])],"isStart":false});
            var Q3;
            Q3=makeQuery(id+"F1.opExtrude","CAP_EDGE",EDGE,{"disambiguationData":[OSD([sQuery(id+"F0.wireOp",EDGE,"E29.trimOffspring")])],"isStart":false});
            var Q4;
            Q4=makeQuery(id+"F1.opExtrude","CAP_EDGE",EDGE,{"disambiguationData":[OSD([sQuery(id+"F0.wireOp",EDGE,"E30.trimOffspring")])],"isStart":false});
            var Q5;
            Q5=makeQuery(id+"F1.opExtrude","CAP_EDGE",EDGE,{"disambiguationData":[OSD([sQuery(id+"F0.wireOp",EDGE,"E31.trimOffspring")])],"isStart":false});
            var Q6;
            Q6=makeQuery(id+"F1.opExtrude","CAP_EDGE",EDGE,{"disambiguationData":[OSD([sQuery(id+"F0.wireOp",EDGE,"E32.trimOffspring")])],"isStart":false});
            var Q7;
            Q7=makeQuery(id+"F1.opExtrude","CAP_EDGE",EDGE,{"disambiguationData":[OSD([sQuery(id+"F0.wireOp",EDGE,"E2")])],"isStart":false});
            chamfer(context, id + "F18", {"entities" : qUnion([Q0, Q1, Q2, Q3, Q4, Q5, Q6, Q7]), "width" : 2.54 * mm, "tangentPropagation" : true});
        }
        {
            var Q0;
            Q0=makeQuery(id+"F1.opExtrude","CAP_EDGE",EDGE,{"disambiguationData":[OSD([sQuery(id+"F0.wireOp",EDGE,"E0.bottom")])],"isStart":false});
            var Q1;
            Q1=makeQuery(id+"F1.opExtrude","CAP_EDGE",EDGE,{"disambiguationData":[OSD([sQuery(id+"F0.wireOp",EDGE,"E0.left")])],"isStart":false});
            var Q2;
            Q2=makeQuery(id+"F1.opExtrude","CAP_EDGE",EDGE,{"disambiguationData":[OSD([sQuery(id+"F0.wireOp",EDGE,"E0.top")])],"isStart":false});
            var Q3;
            Q3=makeQuery(id+"F1.opExtrude","CAP_EDGE",EDGE,{"disambiguationData":[OSD([sQuery(id+"F0.wireOp",EDGE,"E0.right")])],"isStart":false});
            var Q4;
            Q4=makeQuery(id+"F1.opExtrude","CAP_EDGE",EDGE,{"disambiguationData":[OSD([sQuery(id+"F0.wireOp",EDGE,"E4.trimOffspring")])],"isStart":true});
            var Q5;
            Q5=makeQuery(id+"F1.opExtrude","CAP_EDGE",EDGE,{"disambiguationData":[OSD([sQuery(id+"F0.wireOp",EDGE,"E4.trimOffspring")])],"isStart":false});
            chamfer(context, id + "F19", {"entities" : qUnion([Q0, Q1, Q2, Q3, Q4, Q5]), "width" : 1.27 * mm, "tangentPropagation" : true});
        }
        {
            var Q0;
            Q0=makeQuery(id+"F1.opExtrude","CAP_EDGE",EDGE,{"disambiguationData":[OSD([sQuery(id+"F0.wireOp",EDGE,"E3.trimOffspring")])],"isStart":false});
            var Q1;
            Q1=makeQuery(id+"F1.opExtrude","CAP_EDGE",EDGE,{"disambiguationData":[OSD([sQuery(id+"F0.wireOp",EDGE,"E1")])],"isStart":false});
            chamfer(context, id + "F20", {"entities" : qUnion([Q0, Q1]), "width" : 1.27 * mm, "tangentPropagation" : true});
        }
        {
            var Q0;
            Q0=makeQuery(id+"F1.opExtrude","CAP_EDGE",EDGE,{"disambiguationData":[OSD([sQuery(id+"F0.wireOp",EDGE,"E5")])],"isStart":false});
            var Q1;
            Q1=makeQuery(id+"F1.opExtrude","CAP_EDGE",EDGE,{"disambiguationData":[OSD([sQuery(id+"F0.wireOp",EDGE,"E19.filletArc")])],"isStart":false});
            var Q2;
            Q2=makeQuery(id+"F1.opExtrude","CAP_EDGE",EDGE,{"disambiguationData":[OSD([sQuery(id+"F0.wireOp",EDGE,"E7")])],"isStart":false});
            var Q3;
            Q3=makeQuery(id+"F1.opExtrude","CAP_EDGE",EDGE,{"disambiguationData":[OSD([sQuery(id+"F0.wireOp",EDGE,"E20.filletArc")])],"isStart":false});
            var Q4;
            Q4=makeQuery(id+"F1.opExtrude","CAP_EDGE",EDGE,{"disambiguationData":[OSD([sQuery(id+"F0.wireOp",EDGE,"E9")])],"isStart":false});
            var Q5;
            Q5=makeQuery(id+"F1.opExtrude","CAP_EDGE",EDGE,{"disambiguationData":[OSD([sQuery(id+"F0.wireOp",EDGE,"E21.filletArc")])],"isStart":false});
            var Q6;
            Q6=makeQuery(id+"F1.opExtrude","CAP_EDGE",EDGE,{"disambiguationData":[OSD([sQuery(id+"F0.wireOp",EDGE,"E10")])],"isStart":false});
            var Q7;
            Q7=makeQuery(id+"F1.opExtrude","CAP_EDGE",EDGE,{"disambiguationData":[OSD([sQuery(id+"F0.wireOp",EDGE,"E11")])],"isStart":false});
            var Q8;
            Q8=makeQuery(id+"F1.opExtrude","CAP_EDGE",EDGE,{"disambiguationData":[OSD([sQuery(id+"F0.wireOp",EDGE,"E13")])],"isStart":false});
            var Q9;
            Q9=makeQuery(id+"F1.opExtrude","CAP_EDGE",EDGE,{"disambiguationData":[OSD([sQuery(id+"F0.wireOp",EDGE,"E23.filletArc")])],"isStart":false});
            var Q10;
            Q10=makeQuery(id+"F1.opExtrude","CAP_EDGE",EDGE,{"disambiguationData":[OSD([sQuery(id+"F0.wireOp",EDGE,"E15")])],"isStart":false});
            var Q11;
            Q11=makeQuery(id+"F1.opExtrude","CAP_EDGE",EDGE,{"disambiguationData":[OSD([sQuery(id+"F0.wireOp",EDGE,"E24.filletArc")])],"isStart":false});
            var Q12;
            Q12=makeQuery(id+"F1.opExtrude","CAP_EDGE",EDGE,{"disambiguationData":[OSD([sQuery(id+"F0.wireOp",EDGE,"E16")])],"isStart":false});
            var Q13;
            Q13=makeQuery(id+"F1.opExtrude","CAP_EDGE",EDGE,{"disambiguationData":[OSD([sQuery(id+"F0.wireOp",EDGE,"E17")])],"isStart":false});
            var Q14;
            Q14=makeQuery(id+"F1.opExtrude","CAP_EDGE",EDGE,{"disambiguationData":[OSD([sQuery(id+"F0.wireOp",EDGE,"E25.filletArc")])],"isStart":false});
            var Q15;
            Q15=makeQuery(id+"F1.opExtrude","CAP_EDGE",EDGE,{"disambiguationData":[OSD([sQuery(id+"F0.wireOp",EDGE,"E18")])],"isStart":false});
            chamfer(context, id + "F21", {"entities" : qUnion([Q0, Q1, Q2, Q3, Q4, Q5, Q6, Q7, Q8, Q9, Q10, Q11, Q12, Q13, Q14, Q15]), "width" : 2.54 * mm, "tangentPropagation" : true});
        }
        {
            var Q0;
            Q0=qCreatedBy(makeId("Front.planeOp"),FACE);
            var sketch = newSketch(context, id + "F22", { "sketchPlane" : qUnion([Q0])});
            skLineSegment(sketch, "E41", {"start": v(51.99, -63.8) * mm, "end": v(41.6, -56.1) * mm});
            skLineSegment(sketch, "E42", {"start": v(41.6, -56.1) * mm, "end": v(40.95, -58.18) * mm});
            skLineSegment(sketch, "E43", {"start": v(40.95, -58.18) * mm, "end": v(42.7, -59.48) * mm});
            skLineSegment(sketch, "E44", {"start": v(42.7, -59.48) * mm, "end": v(42.7, -62.19) * mm});
            skLineSegment(sketch, "E45", {"start": v(42.7, -62.19) * mm, "end": v(44.26, -64.09) * mm});
            skLineSegment(sketch, "E46", {"start": v(44.26, -64.09) * mm, "end": v(44.26, -69.2) * mm});
            skLineSegment(sketch, "E47", {"start": v(44.26, -69.2) * mm, "end": v(51.98, -69.2) * mm});
            skLineSegment(sketch, "E48", {"start": v(51.98, -69.2) * mm, "end": v(51.99, -63.8) * mm});
            skLineSegment(sketch, "E49", {"start": v(57.84, -67.7) * mm, "end": v(57.84, -57.7) * mm});
            skLineSegment(sketch, "E50", {"start": v(57.84, -57.7) * mm, "end": v(18.83, -21.5) * mm});
            skLineSegment(sketch, "E51", {"start": v(18.83, -21.5) * mm, "end": v(16.3, -6.8) * mm});
            skLineSegment(sketch, "E52", {"start": v(16.3, -6.8) * mm, "end": v(15.02, -8.55) * mm});
            skLineSegment(sketch, "E53", {"start": v(15.02, -8.55) * mm, "end": v(10.2, -9.62) * mm});
            skLineSegment(sketch, "E54", {"start": v(0.53, -62.67) * mm, "end": v(2.75, -62.9) * mm});
            skLineSegment(sketch, "E55", {"start": v(2.75, -62.9) * mm, "end": v(2.75, -71.78) * mm});
            skLineSegment(sketch, "E56", {"start": v(2.75, -71.78) * mm, "end": v(4.74, -71.78) * mm});
            skLineSegment(sketch, "E57", {"start": v(4.74, -71.78) * mm, "end": v(4.74, -62.73) * mm});
            skLineSegment(sketch, "E58", {"start": v(4.74, -62.73) * mm, "end": v(6.37, -61.4) * mm});
            skLineSegment(sketch, "E59", {"start": v(6.37, -61.4) * mm, "end": v(6.37, -49.24) * mm});
            skLineSegment(sketch, "E60", {"start": v(6.37, -49.24) * mm, "end": v(10.67, -49.24) * mm});
            skLineSegment(sketch, "E61", {"start": v(10.67, -49.24) * mm, "end": v(15.57, -32.92) * mm});
            skLineSegment(sketch, "E62", {"start": v(15.57, -32.92) * mm, "end": v(34.7, -50.13) * mm});
            skLineSegment(sketch, "E63", {"start": v(34.7, -50.13) * mm, "end": v(29.5, -71.78) * mm});
            skLineSegment(sketch, "E64", {"start": v(29.5, -71.78) * mm, "end": v(33.96, -71.78) * mm});
            skLineSegment(sketch, "E65", {"start": v(33.96, -71.78) * mm, "end": v(33.96, -70.3) * mm});
            skLineSegment(sketch, "E66", {"start": v(33.96, -70.3) * mm, "end": v(36.63, -70.3) * mm});
            skLineSegment(sketch, "E67", {"start": v(36.63, -70.3) * mm, "end": v(36.63, -71.93) * mm});
            skLineSegment(sketch, "E68", {"start": v(36.63, -71.93) * mm, "end": v(65.7, -71.93) * mm});
            skLineSegment(sketch, "E69", {"start": v(65.7, -71.93) * mm, "end": v(65.7, -67.93) * mm});
            skLineSegment(sketch, "E70", {"start": v(65.7, -67.93) * mm, "end": v(57.84, -67.7) * mm});
            skLineSegment(sketch, "E71", {"start": v(0.53, -62.67) * mm, "end": v(0.53, -51.09) * mm});
            skLineSegment(sketch, "E72", {"start": v(1.54, -47.67) * mm, "end": v(1.54, -61.51) * mm});
            skLineSegment(sketch, "E73", {"start": v(1.54, -61.51) * mm, "end": v(5.66, -60.89) * mm});
            skLineSegment(sketch, "E74", {"start": v(5.66, -60.89) * mm, "end": v(5.66, -49.29) * mm});
            skLineSegment(sketch, "E75", {"start": v(5.66, -49.29) * mm, "end": v(1.54, -47.67) * mm});
            skArc(sketch, "E76", {"start": v(10.2, -9.62) * mm, "mid": v(1.82, -29.53) * mm, "end": v(0.53, -51.09) * mm});
            skSolve(sketch);
        }
        {
            var Q0;
            Q0=makeQuery(id+"F22.imprint","IMPRINT",FACE,{"disambiguationData":[TD([[makeQuery(id+"F22.imprint","IMPRINT",EDGE,{"derivedFrom":sQuery(id+"F22.wireOp",EDGE,"E41")}),-1.0]])]});
            extrude(context, id + "F23", {"entities" : qUnion([Q0]), "depth" : 5.08 * mm, "offsetDistance" : 25.4 * mm});
        }
        {
            var Q0;
            Q0=qCreatedBy(makeId("Front.planeOp"),FACE);
            var sketch = newSketch(context, id + "F24", { "sketchPlane" : qUnion([Q0])});
            skLineSegment(sketch, "E77", {"start": v(67.2, -71.8) * mm, "end": v(73.73, -15.87) * mm});
            skLineSegment(sketch, "E78", {"start": v(73.73, -15.87) * mm, "end": v(69.53, -15.38) * mm});
            skLineSegment(sketch, "E79", {"start": v(69.53, -15.38) * mm, "end": v(69.87, -11.71) * mm});
            skLineSegment(sketch, "E80", {"start": v(69.87, -11.71) * mm, "end": v(76.7, -4) * mm});
            skLineSegment(sketch, "E81", {"start": v(76.7, -4) * mm, "end": v(76.7, -0.14) * mm});
            skLineSegment(sketch, "E82", {"start": v(76.7, -0.14) * mm, "end": v(74.62, 1.34) * mm});
            skLineSegment(sketch, "E83", {"start": v(74.62, 1.34) * mm, "end": v(74.62, 5.5) * mm});
            skLineSegment(sketch, "E84", {"start": v(74.62, 5.5) * mm, "end": v(79.96, 10.83) * mm});
            skLineSegment(sketch, "E85", {"start": v(79.96, 10.83) * mm, "end": v(85.74, 7.72) * mm});
            skLineSegment(sketch, "E86", {"start": v(85.74, 7.72) * mm, "end": v(85.74, -5.48) * mm});
            skLineSegment(sketch, "E87", {"start": v(85.74, -5.48) * mm, "end": v(92.72, -7.86) * mm});
            skLineSegment(sketch, "E88", {"start": v(92.72, -7.86) * mm, "end": v(87.82, -16.46) * mm});
            skLineSegment(sketch, "E89", {"start": v(87.82, -16.46) * mm, "end": v(92.72, -63.78) * mm});
            skLineSegment(sketch, "E90", {"start": v(92.72, -63.78) * mm, "end": v(96.32, -63.4) * mm});
            skLineSegment(sketch, "E91", {"start": v(96.32, -63.4) * mm, "end": v(96.8, -68.05) * mm});
            skLineSegment(sketch, "E92", {"start": v(96.8, -68.05) * mm, "end": v(92.27, -71.8) * mm});
            skLineSegment(sketch, "E93", {"start": v(92.27, -71.8) * mm, "end": v(67.2, -71.8) * mm});
            skSolve(sketch);
        }
        {
            var Q0;
            Q0=makeQuery(id+"F24.imprint","IMPRINT",FACE,{"disambiguationData":[TD([[makeQuery(id+"F24.imprint","IMPRINT",EDGE,{"derivedFrom":sQuery(id+"F24.wireOp",EDGE,"E77")}),-1.0]])]});
            extrude(context, id + "F25", {"entities" : qUnion([Q0]), "depth" : 5.08 * mm, "offsetDistance" : 25.4 * mm});
        }
        {
            var Q0;
            Q0=makeQuery(id+"F25.opExtrude","CAP_FACE",FACE,{"disambiguationData":[OSD([sQuery(id+"F24.wireOp",EDGE,"E77"),sQuery(id+"F24.wireOp",EDGE,"E78"),sQuery(id+"F24.wireOp",EDGE,"E79"),sQuery(id+"F24.wireOp",EDGE,"E80"),sQuery(id+"F24.wireOp",EDGE,"E81"),sQuery(id+"F24.wireOp",EDGE,"E82"),sQuery(id+"F24.wireOp",EDGE,"E83"),sQuery(id+"F24.wireOp",EDGE,"E84"),sQuery(id+"F24.wireOp",EDGE,"E85"),sQuery(id+"F24.wireOp",EDGE,"E86"),sQuery(id+"F24.wireOp",EDGE,"E87"),sQuery(id+"F24.wireOp",EDGE,"E88"),sQuery(id+"F24.wireOp",EDGE,"E89"),sQuery(id+"F24.wireOp",EDGE,"E90"),sQuery(id+"F24.wireOp",EDGE,"E91"),sQuery(id+"F24.wireOp",EDGE,"E92"),sQuery(id+"F24.wireOp",EDGE,"E93")])],"isStart":false});
            var sketch = newSketch(context, id + "F26", { "sketchPlane" : qUnion([Q0])});
            skLineSegment(sketch, "E94", {"start": v(80.2, 9.6) * mm, "end": v(80.2, 8.06) * mm});
            skLineSegment(sketch, "E95", {"start": v(80.2, 8.06) * mm, "end": v(81.59, 8.06) * mm});
            skLineSegment(sketch, "E96", {"start": v(81.59, 8.06) * mm, "end": v(81.59, 9.12) * mm});
            skLineSegment(sketch, "E97", {"start": v(81.59, 9.12) * mm, "end": v(80.2, 9.6) * mm});
            skLineSegment(sketch, "E98", {"start": v(80.79, 5.55) * mm, "end": v(79.61, 4.97) * mm});
            skLineSegment(sketch, "E99", {"start": v(79.61, 4.97) * mm, "end": v(78.65, 4.97) * mm});
            skLineSegment(sketch, "E100", {"start": v(78.65, 4.97) * mm, "end": v(78.65, 3) * mm});
            skLineSegment(sketch, "E101", {"start": v(78.65, 3) * mm, "end": v(80.2, 3) * mm});
            skLineSegment(sketch, "E102", {"start": v(80.2, 3) * mm, "end": v(82.07, 4.27) * mm});
            skLineSegment(sketch, "E103", {"start": v(82.07, 4.27) * mm, "end": v(80.79, 5.55) * mm});
            skLineSegment(sketch, "E104", {"start": v(77.96, -0.74) * mm, "end": v(77.96, -2.87) * mm});
            skLineSegment(sketch, "E105", {"start": v(77.96, -2.87) * mm, "end": v(79.03, -3.72) * mm});
            skLineSegment(sketch, "E106", {"start": v(79.03, -3.72) * mm, "end": v(79.03, -0.69) * mm});
            skLineSegment(sketch, "E107", {"start": v(79.03, -0.69) * mm, "end": v(77.96, -0.74) * mm});
            skLineSegment(sketch, "E108", {"start": v(82.33, 0.6) * mm, "end": v(82.33, -0.74) * mm});
            skLineSegment(sketch, "E109", {"start": v(82.33, -0.74) * mm, "end": v(83.93, -0.85) * mm});
            skLineSegment(sketch, "E110", {"start": v(83.93, -0.85) * mm, "end": v(83.93, 0.7) * mm});
            skLineSegment(sketch, "E111", {"start": v(83.93, 0.7) * mm, "end": v(82.33, 0.6) * mm});
            skLineSegment(sketch, "E112", {"start": v(82.33, -2.23) * mm, "end": v(83.88, -2.23) * mm});
            skLineSegment(sketch, "E113", {"start": v(83.88, -2.23) * mm, "end": v(83.88, -3.94) * mm});
            skLineSegment(sketch, "E114", {"start": v(83.88, -3.94) * mm, "end": v(82.33, -3.35) * mm});
            skLineSegment(sketch, "E115", {"start": v(82.33, -3.35) * mm, "end": v(82.33, -2.23) * mm});
            skLineSegment(sketch, "E116", {"start": v(75.8, -53.72) * mm, "end": v(75.8, -56.64) * mm});
            skLineSegment(sketch, "E117", {"start": v(75.8, -56.64) * mm, "end": v(80.2, -60.44) * mm});
            skLineSegment(sketch, "E118", {"start": v(80.2, -60.44) * mm, "end": v(80.2, -54.23) * mm});
            skLineSegment(sketch, "E119", {"start": v(80.2, -54.23) * mm, "end": v(75.8, -53.72) * mm});
            skLineSegment(sketch, "E120", {"start": v(80.79, -52.07) * mm, "end": v(75.8, -50.17) * mm});
            skLineSegment(sketch, "E121", {"start": v(75.8, -50.17) * mm, "end": v(75.8, -45.73) * mm});
            skLineSegment(sketch, "E122", {"start": v(75.8, -45.73) * mm, "end": v(80.79, -42.56) * mm});
            skLineSegment(sketch, "E123", {"start": v(80.79, -42.56) * mm, "end": v(80.79, -52.07) * mm});
            skLineSegment(sketch, "E124", {"start": v(80.79, -40.44) * mm, "end": v(75.8, -43.9) * mm});
            skLineSegment(sketch, "E125", {"start": v(75.8, -43.9) * mm, "end": v(75.8, -38.41) * mm});
            skLineSegment(sketch, "E126", {"start": v(75.8, -38.41) * mm, "end": v(80.79, -40.44) * mm});
            skLineSegment(sketch, "E127", {"start": v(80.79, -37.13) * mm, "end": v(78.65, -35.37) * mm});
            skLineSegment(sketch, "E128", {"start": v(78.65, -35.37) * mm, "end": v(78.65, -32.12) * mm});
            skLineSegment(sketch, "E129", {"start": v(78.65, -32.12) * mm, "end": v(80.79, -30.84) * mm});
            skLineSegment(sketch, "E130", {"start": v(80.79, -30.84) * mm, "end": v(80.79, -37.13) * mm});
            skLineSegment(sketch, "E131", {"start": v(78.65, -25.29) * mm, "end": v(78.65, -29.77) * mm});
            skLineSegment(sketch, "E132", {"start": v(78.65, -29.77) * mm, "end": v(81.16, -27.74) * mm});
            skLineSegment(sketch, "E133", {"start": v(81.16, -27.74) * mm, "end": v(78.65, -25.29) * mm});
            skLineSegment(sketch, "E134", {"start": v(79.61, -22.16) * mm, "end": v(82.33, -24.87) * mm});
            skLineSegment(sketch, "E135", {"start": v(82.33, -24.87) * mm, "end": v(82.33, -21.6) * mm});
            skLineSegment(sketch, "E136", {"start": v(82.33, -21.6) * mm, "end": v(84.32, -21.6) * mm});
            skLineSegment(sketch, "E137", {"start": v(84.32, -21.6) * mm, "end": v(84.32, -19.4) * mm});
            skLineSegment(sketch, "E138", {"start": v(84.32, -19.4) * mm, "end": v(81.16, -18.92) * mm});
            skLineSegment(sketch, "E139", {"start": v(81.16, -18.92) * mm, "end": v(79.61, -22.16) * mm});
            skLineSegment(sketch, "E140", {"start": v(75.09, -19.18) * mm, "end": v(75.09, -22.57) * mm});
            skLineSegment(sketch, "E141", {"start": v(75.09, -22.57) * mm, "end": v(75.8, -22.84) * mm});
            skLineSegment(sketch, "E142", {"start": v(75.8, -22.84) * mm, "end": v(75.8, -19.07) * mm});
            skLineSegment(sketch, "E143", {"start": v(75.8, -19.07) * mm, "end": v(75.09, -19.18) * mm});
            skLineSegment(sketch, "E144", {"start": v(83, -54.61) * mm, "end": v(83, -60.95) * mm});
            skLineSegment(sketch, "E145", {"start": v(83, -60.95) * mm, "end": v(86.47, -60.95) * mm});
            skLineSegment(sketch, "E146", {"start": v(86.47, -60.95) * mm, "end": v(86.47, -55.52) * mm});
            skLineSegment(sketch, "E147", {"start": v(86.47, -55.52) * mm, "end": v(83, -54.61) * mm});
            skLineSegment(sketch, "E148", {"start": v(85.74, -52.8) * mm, "end": v(87.83, -51) * mm});
            skLineSegment(sketch, "E149", {"start": v(87.83, -51) * mm, "end": v(88.92, -51.41) * mm});
            skLineSegment(sketch, "E150", {"start": v(88.92, -51.41) * mm, "end": v(88.92, -52.96) * mm});
            skLineSegment(sketch, "E151", {"start": v(88.92, -52.96) * mm, "end": v(85.74, -52.8) * mm});
            skLineSegment(sketch, "E152", {"start": v(86.7, -47) * mm, "end": v(86.7, -49.19) * mm});
            skLineSegment(sketch, "E153", {"start": v(86.7, -49.19) * mm, "end": v(88.34, -49.81) * mm});
            skLineSegment(sketch, "E154", {"start": v(88.34, -49.81) * mm, "end": v(88.43, -47.3) * mm});
            skLineSegment(sketch, "E155", {"start": v(88.43, -47.3) * mm, "end": v(86.7, -47) * mm});
            skLineSegment(sketch, "E156", {"start": v(83, -44.44) * mm, "end": v(83, -48.13) * mm});
            skLineSegment(sketch, "E157", {"start": v(83, -48.13) * mm, "end": v(84.81, -47.23) * mm});
            skLineSegment(sketch, "E158", {"start": v(84.81, -47.23) * mm, "end": v(85.11, -44.51) * mm});
            skLineSegment(sketch, "E159", {"start": v(85.11, -44.51) * mm, "end": v(83, -44.44) * mm});
            skLineSegment(sketch, "E160", {"start": v(84.44, -39.38) * mm, "end": v(84.44, -40.44) * mm});
            skLineSegment(sketch, "E161", {"start": v(84.44, -40.44) * mm, "end": v(88.2, -40.44) * mm});
            skLineSegment(sketch, "E162", {"start": v(88.2, -40.44) * mm, "end": v(88.2, -37.73) * mm});
            skLineSegment(sketch, "E163", {"start": v(88.2, -37.73) * mm, "end": v(84.44, -39.38) * mm});
            skLineSegment(sketch, "E164", {"start": v(84.44, -31.1) * mm, "end": v(84.44, -36.3) * mm});
            skLineSegment(sketch, "E165", {"start": v(84.44, -36.3) * mm, "end": v(87.68, -36.3) * mm});
            skLineSegment(sketch, "E166", {"start": v(87.68, -36.3) * mm, "end": v(87.68, -29.5) * mm});
            skLineSegment(sketch, "E167", {"start": v(87.68, -29.5) * mm, "end": v(84.44, -31.1) * mm});
            skLineSegment(sketch, "E168", {"start": v(85.74, -22.16) * mm, "end": v(83.91, -26.96) * mm});
            skLineSegment(sketch, "E169", {"start": v(83.91, -26.96) * mm, "end": v(86.7, -26.96) * mm});
            skLineSegment(sketch, "E170", {"start": v(86.7, -26.96) * mm, "end": v(85.74, -22.16) * mm});
            skSolve(sketch);
        }
        {
            var Q0;
            Q0=makeQuery(id+"F26.imprint","IMPRINT",FACE,{"disambiguationData":[TD([[makeQuery(id+"F26.imprint","IMPRINT",EDGE,{"derivedFrom":sQuery(id+"F26.wireOp",EDGE,"E94")}),1.0]])]});
            var Q1;
            Q1=makeQuery(id+"F26.imprint","IMPRINT",FACE,{"disambiguationData":[TD([[makeQuery(id+"F26.imprint","IMPRINT",EDGE,{"derivedFrom":sQuery(id+"F26.wireOp",EDGE,"E98")}),1.0]])]});
            var Q2;
            Q2=makeQuery(id+"F26.imprint","IMPRINT",FACE,{"disambiguationData":[TD([[makeQuery(id+"F26.imprint","IMPRINT",EDGE,{"derivedFrom":sQuery(id+"F26.wireOp",EDGE,"E104")}),1.0]])]});
            var Q3;
            Q3=makeQuery(id+"F26.imprint","IMPRINT",FACE,{"disambiguationData":[TD([[makeQuery(id+"F26.imprint","IMPRINT",EDGE,{"derivedFrom":sQuery(id+"F26.wireOp",EDGE,"E108")}),1.0]])]});
            var Q4;
            Q4=makeQuery(id+"F26.imprint","IMPRINT",FACE,{"disambiguationData":[TD([[makeQuery(id+"F26.imprint","IMPRINT",EDGE,{"derivedFrom":sQuery(id+"F26.wireOp",EDGE,"E112")}),-1.0]])]});
            var Q5;
            Q5=makeQuery(id+"F26.imprint","IMPRINT",FACE,{"disambiguationData":[TD([[makeQuery(id+"F26.imprint","IMPRINT",EDGE,{"derivedFrom":sQuery(id+"F26.wireOp",EDGE,"E140")}),1.0]])]});
            var Q6;
            Q6=makeQuery(id+"F26.imprint","IMPRINT",FACE,{"disambiguationData":[TD([[makeQuery(id+"F26.imprint","IMPRINT",EDGE,{"derivedFrom":sQuery(id+"F26.wireOp",EDGE,"E134")}),1.0]])]});
            var Q7;
            Q7=makeQuery(id+"F26.imprint","IMPRINT",FACE,{"disambiguationData":[TD([[makeQuery(id+"F26.imprint","IMPRINT",EDGE,{"derivedFrom":sQuery(id+"F26.wireOp",EDGE,"E131")}),1.0]])]});
            var Q8;
            Q8=makeQuery(id+"F26.imprint","IMPRINT",FACE,{"disambiguationData":[TD([[makeQuery(id+"F26.imprint","IMPRINT",EDGE,{"derivedFrom":sQuery(id+"F26.wireOp",EDGE,"E168")}),1.0]])]});
            var Q9;
            Q9=makeQuery(id+"F26.imprint","IMPRINT",FACE,{"disambiguationData":[TD([[makeQuery(id+"F26.imprint","IMPRINT",EDGE,{"derivedFrom":sQuery(id+"F26.wireOp",EDGE,"E164")}),1.0]])]});
            var Q10;
            Q10=makeQuery(id+"F26.imprint","IMPRINT",FACE,{"disambiguationData":[TD([[makeQuery(id+"F26.imprint","IMPRINT",EDGE,{"derivedFrom":sQuery(id+"F26.wireOp",EDGE,"E127")}),-1.0]])]});
            var Q11;
            Q11=makeQuery(id+"F26.imprint","IMPRINT",FACE,{"disambiguationData":[TD([[makeQuery(id+"F26.imprint","IMPRINT",EDGE,{"derivedFrom":sQuery(id+"F26.wireOp",EDGE,"E124")}),-1.0]])]});
            var Q12;
            Q12=makeQuery(id+"F26.imprint","IMPRINT",FACE,{"disambiguationData":[TD([[makeQuery(id+"F26.imprint","IMPRINT",EDGE,{"derivedFrom":sQuery(id+"F26.wireOp",EDGE,"E160")}),1.0]])]});
            var Q13;
            Q13=makeQuery(id+"F26.imprint","IMPRINT",FACE,{"disambiguationData":[TD([[makeQuery(id+"F26.imprint","IMPRINT",EDGE,{"derivedFrom":sQuery(id+"F26.wireOp",EDGE,"E120")}),-1.0]])]});
            var Q14;
            Q14=makeQuery(id+"F26.imprint","IMPRINT",FACE,{"disambiguationData":[TD([[makeQuery(id+"F26.imprint","IMPRINT",EDGE,{"derivedFrom":sQuery(id+"F26.wireOp",EDGE,"E156")}),1.0]])]});
            var Q15;
            Q15=makeQuery(id+"F26.imprint","IMPRINT",FACE,{"disambiguationData":[TD([[makeQuery(id+"F26.imprint","IMPRINT",EDGE,{"derivedFrom":sQuery(id+"F26.wireOp",EDGE,"E116")}),1.0]])]});
            var Q16;
            Q16=makeQuery(id+"F26.imprint","IMPRINT",FACE,{"disambiguationData":[TD([[makeQuery(id+"F26.imprint","IMPRINT",EDGE,{"derivedFrom":sQuery(id+"F26.wireOp",EDGE,"E144")}),1.0]])]});
            var Q17;
            Q17=makeQuery(id+"F26.imprint","IMPRINT",FACE,{"disambiguationData":[TD([[makeQuery(id+"F26.imprint","IMPRINT",EDGE,{"derivedFrom":sQuery(id+"F26.wireOp",EDGE,"E148")}),-1.0]])]});
            var Q18;
            Q18=makeQuery(id+"F26.imprint","IMPRINT",FACE,{"disambiguationData":[TD([[makeQuery(id+"F26.imprint","IMPRINT",EDGE,{"derivedFrom":sQuery(id+"F26.wireOp",EDGE,"E152")}),1.0]])]});
            extrude(context, id + "F27", {"entities" : qUnion([Q0, Q1, Q2, Q3, Q4, Q5, Q6, Q7, Q8, Q9, Q10, Q11, Q12, Q13, Q14, Q15, Q16, Q17, Q18]), "operationType" : NewBodyOperationType.REMOVE, "oppositeDirection" : true, "depth" : 25.4 * mm, "offsetDistance" : 25.4 * mm});
        }
    });
